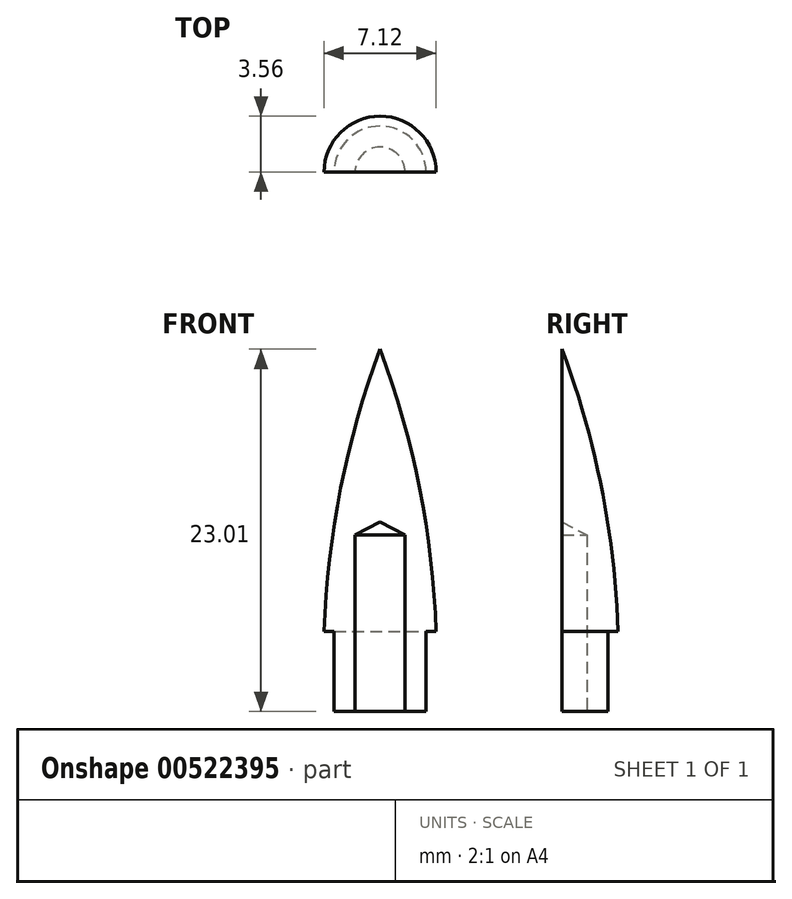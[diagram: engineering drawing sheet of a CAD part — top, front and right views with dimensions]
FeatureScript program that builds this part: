
annotation { "Feature Type Name" : "Feature", "Feature Type Description" : "" }
export const myFeature = defineFeature(function(context is Context, id is Id, definition is map)
    precondition{}
    {
        {
            var Q0;
            Q0=qCreatedBy(makeId("Front.planeOp"),FACE);
            var sketch = newSketch(context, id + "F0", { "sketchPlane" : qUnion([Q0])});
            skLineSegment(sketch, "E0", {"start": v(2.92, 0) * mm, "end": v(3.56, 0) * mm});
            skArc(sketch, "E1", {"start": v(3.56, 0) * mm, "mid": v(2.5, 9.11) * mm, "end": v(0, 17.93) * mm});
            skPoint(sketch, "E2.orphan", {"position": v(0, 0) * mm});
            skLineSegment(sketch, "E3", {"start": v(2.92, 0) * mm, "end": v(2.92, -1.02) * mm});
            skLineSegment(sketch, "E4", {"start": v(2.92, -1.02) * mm, "end": v(1.59, -1.02) * mm, "construction": true});
            skLineSegment(sketch, "E5", {"start": v(0, 6.97) * mm, "end": v(1.59, 6.13) * mm});
            skLineSegment(sketch, "E6", {"start": v(1.59, 6.13) * mm, "end": v(1.59, -1.02) * mm});
            skLineSegment(sketch, "E7.trimOffspring", {"start": v(0, 6.97) * mm, "end": v(0, 17.93) * mm});
            skLineSegment(sketch, "E8", {"start": v(1.59, -1.02) * mm, "end": v(1.59, -5.08) * mm});
            skLineSegment(sketch, "E9", {"start": v(1.59, -5.08) * mm, "end": v(2.92, -5.08) * mm});
            skLineSegment(sketch, "E10", {"start": v(2.92, -5.08) * mm, "end": v(2.92, -1.02) * mm});
            skSolve(sketch);
        }
        {
            var Q0;
            Q0 = qSketchRegion(id + "F0", true);
            var Q1;
            Q1=sQuery(id+"F0.wireOp",EDGE,"E7.trimOffspring");
            revolve(context, id + "F1", {"surfaceOperationType" : NewSurfaceOperationType.NEW, "entities" : qUnion([Q0]), "axis" : qUnion([Q1]), "revolveType" : RevolveType.ONE_DIRECTION, "angle" : 180 * degree});
        }
    });
